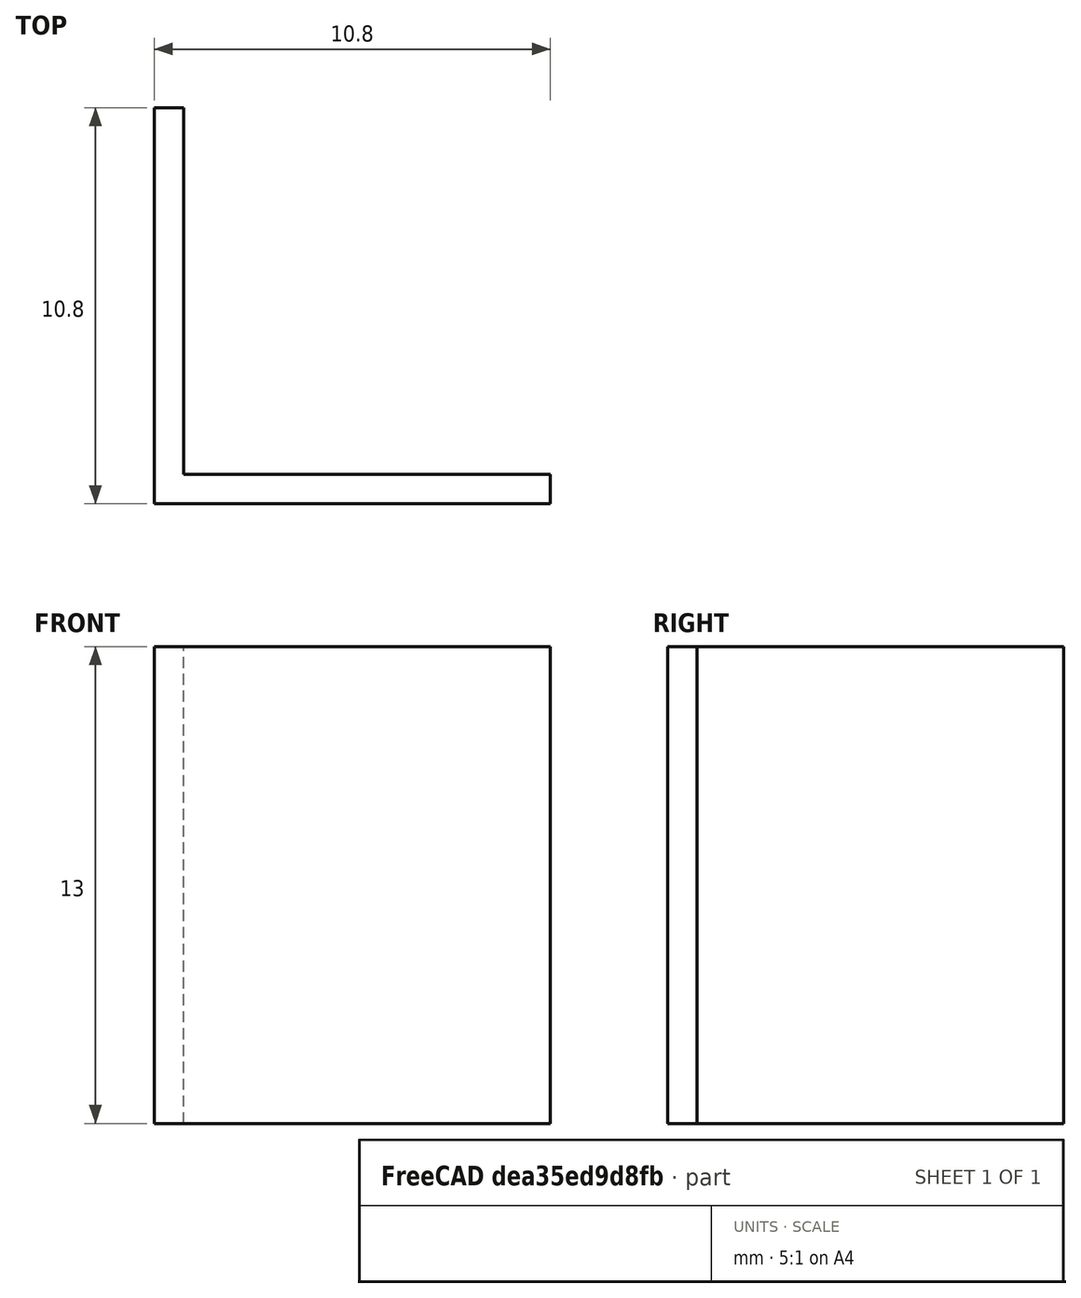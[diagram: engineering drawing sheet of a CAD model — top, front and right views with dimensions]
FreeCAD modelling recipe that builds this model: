
FCSTD DOCUMENT  (FreeCAD 0.16R6710 (Git))
Label: MotorClip
License: All rights reserved
LicenseURL: http://en.wikipedia.org/wiki/All_rights_reserved
objects: Sketcher::SketchObject×1, PartDesign::Pad×1
note: 3 computed .brp shape members not serialized (recipe doc carries the construction recipe); baked Part::Feature solids carry a one-line shape summary decoded from their .brp

FEATURE [Sketcher::SketchObject] Sketch
  sketch-geometry (6):
    g0: LineSegment StartX=0 StartY=0 StartZ=0 EndX=0 EndY=10 EndZ=0
    g1: LineSegment StartX=0 StartY=10 StartZ=0 EndX=-0.8 EndY=10 EndZ=0
    g2: LineSegment StartX=-0.8 StartY=10 StartZ=0 EndX=-0.8 EndY=-0.8 EndZ=0
    g3: LineSegment StartX=-0.8 StartY=-0.8 StartZ=0 EndX=10 EndY=-0.8 EndZ=0
    g4: LineSegment StartX=10 StartY=-0.8 StartZ=0 EndX=10 EndY=0 EndZ=0
    g5: LineSegment StartX=10 StartY=0 StartZ=0 EndX=0 EndY=0 EndZ=0
  constraints (17):
    c: Coincident(g-1,g0)
    c: Vertical(g0)
    c: Coincident(g0,g1)
    c: Horizontal(g1)
    c: Coincident(g1,g2)
    c: Vertical(g2)
    c: Coincident(g2,g3)
    c: Horizontal(g3)
    c: Coincident(g3,g4)
    c: PointOnObject(g4,g-1)
    c: Vertical(g4)
    c: Coincident(g4,g5)
    c: Coincident(g5,g-1)
    c: Equal(g4,g1)
    c: Equal(g0,g5)
    c: Distance(g5) = 10
    c: Distance(g4) = 0.8
FEATURE [PartDesign::Pad] Pad
  Length = 13
  Length2 = 100
  Sketch = -> Sketch
  Type = 0
